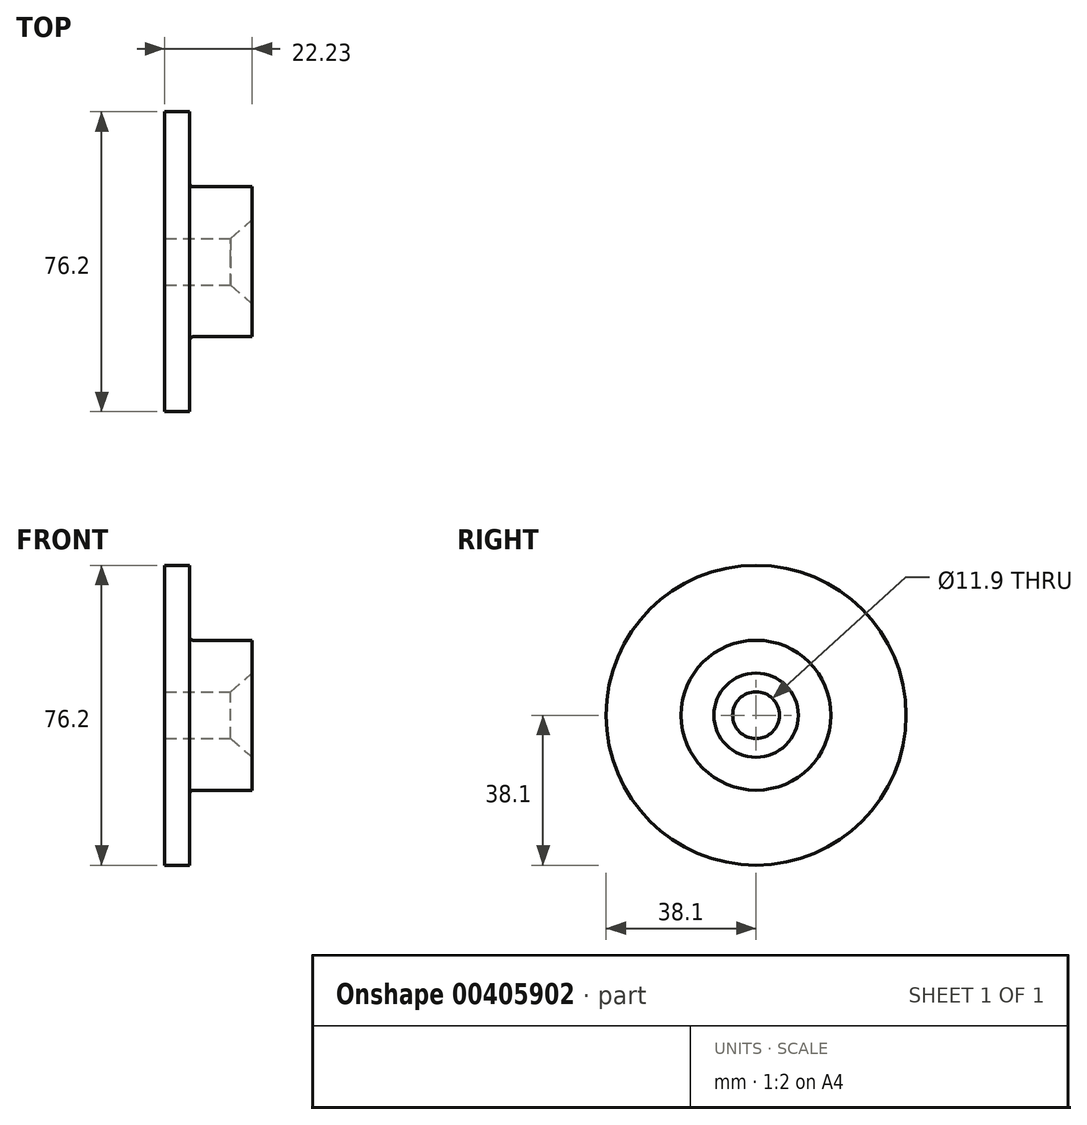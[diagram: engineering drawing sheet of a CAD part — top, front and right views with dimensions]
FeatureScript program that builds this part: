
annotation { "Feature Type Name" : "Feature", "Feature Type Description" : "" }
export const myFeature = defineFeature(function(context is Context, id is Id, definition is map)
    precondition{}
    {
        {
            var Q0;
            Q0=qCreatedBy(makeId("Front.planeOp"),FACE);
            var sketch = newSketch(context, id + "F0", { "sketchPlane" : qUnion([Q0])});
            skLineSegment(sketch, "E0", {"start": v(0, 38.1) * mm, "end": v(6.35, 38.1) * mm});
            skLineSegment(sketch, "E1", {"start": v(6.35, 38.1) * mm, "end": v(6.35, 19.05) * mm});
            skLineSegment(sketch, "E2", {"start": v(6.35, 19.05) * mm, "end": v(22.23, 19.05) * mm});
            skLineSegment(sketch, "E3", {"start": v(22.23, 19.05) * mm, "end": v(22.23, 0) * mm});
            skLineSegment(sketch, "E4", {"start": v(22.23, 0) * mm, "end": v(0, 0) * mm});
            skLineSegment(sketch, "E5", {"start": v(0, 0) * mm, "end": v(0, 38.1) * mm});
            skSolve(sketch);
        }
        {
            var Q0;
            Q0=makeQuery(id+"F0.imprint","IMPRINT",FACE,{"disambiguationData":[TD([[makeQuery(id+"F0.imprint","IMPRINT",EDGE,{"derivedFrom":sQuery(id+"F0.wireOp",EDGE,"E0")}),-1.0]])]});
            var Q1;
            Q1=sQuery(id+"F0.wireOp",EDGE,"E4");
            revolve(context, id + "F1", {"entities" : qUnion([Q0]), "axis" : qUnion([Q1]), "revolveType" : RevolveType.FULL});
        }
        {
            var Q0;
            Q0=makeQuery(id+"F1.opRevolve","SWEPT_EDGE",EDGE,{"disambiguationData":[OSD([sQuery(id+"F0.wireOp",EDGE,"E1"),sQuery(id+"F0.wireOp",EDGE,"E2")])]});
            fillet(context, id + "F2", {"entities" : qUnion([Q0]), "radius" : 0.8 * mm, "tangentPropagation" : true, "allowEdgeOverflow" : false});
        }
        {
            var Q0;
            Q0=makeQuery(id+"F1.opRevolve","SWEPT_FACE",FACE,{"disambiguationData":[OSD([sQuery(id+"F0.wireOp",EDGE,"E3")])]});
            var sketch = newSketch(context, id + "F3", { "sketchPlane" : qUnion([Q0])});
            skPoint(sketch, "E6", {"position": v(0, 0) * mm});
            skSolve(sketch);
        }
        {
            var Q0;
            Q0=sQuery(id+"F3.wireOp",VERTEX,"E6");
            var Q1;
            Q1=makeQuery(id+"F1.opRevolve","SWEPT_BODY",BODY,{"disambiguationData":[OSD([sQuery(id+"F0.wireOp",EDGE,"E0"),sQuery(id+"F0.wireOp",EDGE,"E1"),sQuery(id+"F0.wireOp",EDGE,"E2"),sQuery(id+"F0.wireOp",EDGE,"E3"),sQuery(id+"F0.wireOp",EDGE,"E4"),sQuery(id+"F0.wireOp",EDGE,"E5")])]});
            hole(context, id + "F4", {"style" : HoleStyle.C_SINK, "endStyle" : HoleEndStyle.THROUGH, "standardTappedOrClearance" : lookupTablePath({ "standard" : "ANSI", "fit" : "Normal (ASME)", "size" : "7/16", "type" : "Clearance" }), "standardBlindInLast" : lookupTablePath({ "fit" : "Free", "standard" : "ANSI", "size" : "7/16", "type" : "Clearance" }), "holeDiameter" : 11.9 * mm, "cSinkDiameter" : 21.44 * mm, "cSinkAngle" : 82 * degree, "isTappedThrough" : true, "tappedDepth" : 12.7 * mm, "tapClearance" : 3, "locations" : qUnion([Q0]), "scope" : qUnion([Q1])});
        }
    });
